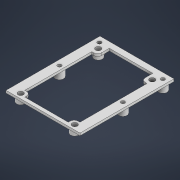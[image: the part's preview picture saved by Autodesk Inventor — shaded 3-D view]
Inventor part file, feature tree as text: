
AUTODESK INVENTOR PART (.ipt)
format: ipt  version: 2021 (Build 250183000, 183)  size: 223,744 bytes
history: native  units: mm
features: extrude x5, sketch x5, fillet x1
ambient origin geometry x8: Origin, YZ Plane, XZ Plane, XY Plane, X Axis, Y Axis, Z Axis, Center Point
bodies: Volumenkörper1 (feature_tree)
feature tree (11):
  extrude  "Extrusion1"  Depth=80.0mm
  sketch  "Skizze3"  dims[d4=27.0mm d5=27.0mm]
  extrude  "Extrusion2"  Depth=3.2mm
  extrude  "Extrusion3"  Depth=27.0mm
  extrude  "Extrusion4"  Depth=5.0mm
  extrude  "Extrusion5"  Depth=3.5mm
  fillet  "Rundung1"  Radius=27.0mm
  sketch  "Skizze1"  dims[d0=63.0mm d1=80.0mm]
  sketch  "Skizze2"  dims[d2=3.2mm d3=3.2mm]
  sketch  "Skizze4"  dims[d6=5.0mm d7=5.0mm]
  sketch  "Skizze5"  dims[d8=3.2mm d9=3.2mm d10=27.0mm d11=27.0mm d12=34.0mm d13=34.0mm d14=2.0mm d15=0.0mm d16=7.0mm d17=7.0mm d18=7.0mm d19=7.0mm d20=6.0mm d21=0.0mm d22=7.0mm d23=7.0mm d24=7.0mm d25=7.0mm d26=23.0mm d27=23.0mm d28=23.0mm d29=23.0mm d31=10.0mm d32=10.0mm d33=66.0mm d34=66.0mm d35=6.0mm d36=0.0mm d37=4.5mm d38=4.5mm d39=4.5mm d40=4.5mm d41=6.0mm d42=0.0mm d43=15.0mm d44=8.0mm d45=8.0mm d46=8.0mm d47=6.0mm d48=0.0mm d49=3.0mm d50=13.0mm d51=13.0mm d52=13.0mm d53=13.0mm d54=5.0mm d55=8.0mm d56=8.0mm d57=15.0mm d58=15.0mm d59=3.5mm]
